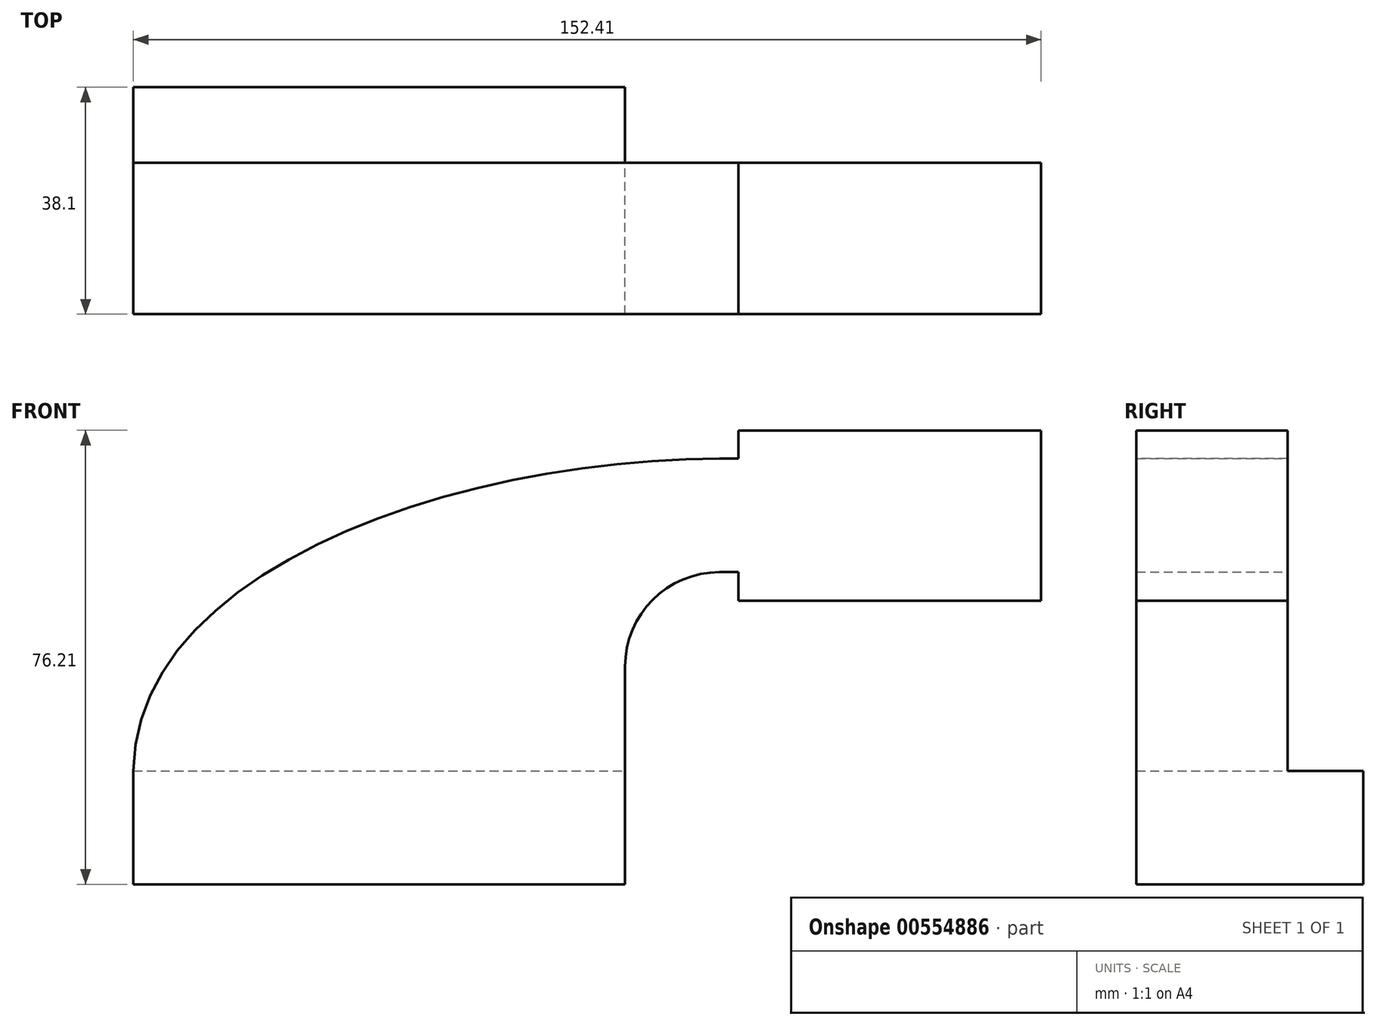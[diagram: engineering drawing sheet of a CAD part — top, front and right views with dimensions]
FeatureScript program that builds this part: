
annotation { "Feature Type Name" : "Feature", "Feature Type Description" : "" }
export const myFeature = defineFeature(function(context is Context, id is Id, definition is map)
    precondition{}
    {
        {
            var Q0;
            Q0=qCreatedBy(makeId("Front.planeOp"),FACE);
            var sketch = newSketch(context, id + "F0", { "sketchPlane" : qUnion([Q0])});
            skLineSegment(sketch, "E0.bottom", {"start": v(-41.28, 9.52) * mm, "end": v(41.27, 9.53) * mm});
            skLineSegment(sketch, "E0.top", {"start": v(-41.28, -9.52) * mm, "end": v(41.28, -9.52) * mm});
            skLineSegment(sketch, "E0.left", {"start": v(-41.28, 9.52) * mm, "end": v(-41.28, -9.53) * mm});
            skLineSegment(sketch, "E0.right", {"start": v(41.27, 9.53) * mm, "end": v(41.28, -9.52) * mm});
            skPoint(sketch, "E0.middle", {"position": v(0, 0) * mm});
            skLineSegment(sketch, "E1.bottom", {"start": v(60.32, 38.1) * mm, "end": v(111.12, 38.1) * mm});
            skLineSegment(sketch, "E1.top", {"start": v(60.32, 66.67) * mm, "end": v(111.12, 66.67) * mm});
            skLineSegment(sketch, "E1.left", {"start": v(60.32, 38.1) * mm, "end": v(60.32, 66.68) * mm});
            skLineSegment(sketch, "E1.right", {"start": v(111.12, 38.1) * mm, "end": v(111.12, 66.68) * mm});
            skPoint(sketch, "E1.middle", {"position": v(85.72, 52.39) * mm});
            skLineSegment(sketch, "E2", {"start": v(41.27, 9.53) * mm, "end": v(41.27, 27) * mm});
            skArc(sketch, "E3", {"start": v(41.27, 27) * mm, "mid": v(45.92, 38.23) * mm, "end": v(57.15, 42.88) * mm});
            skLineSegment(sketch, "E4", {"start": v(57.15, 42.88) * mm, "end": v(74.24, 42.88) * mm});
            skLineSegment(sketch, "E5.0", {"start": v(57.15, 61.93) * mm, "end": v(74.24, 61.93) * mm});
            skArc(sketch, "E5.1", {"start": v(22.22, 27) * mm, "mid": v(32.45, 51.7) * mm, "end": v(57.15, 61.93) * mm});
            skLineSegment(sketch, "E5.2", {"start": v(22.22, 9.53) * mm, "end": v(22.22, 27) * mm});
            skLineSegment(sketch, "E6", {"start": v(85.72, 38.1) * mm, "end": v(85.72, 66.67) * mm});
            skLineSegment(sketch, "E7", {"start": v(74.24, 61.93) * mm, "end": v(85.72, 61.93) * mm});
            skLineSegment(sketch, "E8", {"start": v(74.24, 42.88) * mm, "end": v(85.72, 42.88) * mm});
            skFitSpline(sketch, "E9", {"points": [v(-41.28, 9.52) * mm, v(57.15, 61.93) * mm], "startDerivative": vector(1.43, 103.54) * mm, "endDerivative": vector(128.32, -0.1) * mm});
            skSolve(sketch);
        }
        {
            var Q0;
            Q0=qCreatedBy(makeId("Front.planeOp"),FACE);
            var sketch = newSketch(context, id + "F1", { "sketchPlane" : qUnion([Q0])});
            skSolve(sketch);
        }
        {
            var Q0;
            Q0=makeQuery(id+"F0.imprint","IMPRINT",FACE,{"disambiguationData":[TD([[makeQuery(id+"F0.imprint","IMPRINT",EDGE,{"derivedFrom":sQuery(id+"F0.wireOp",EDGE,"E0.top")}),1.0]])]});
            extrude(context, id + "F2", {"entities" : qUnion([Q0]), "endBound" : BoundingType.SYMMETRIC, "depth" : 25.4 * mm, "offsetDistance" : 25.4 * mm});
        }
        {
            var Q0;
            Q0 = qSketchRegion(id + "F0XvRdL9u1ZFRl4_1", true);
            var Q1;
            Q1 = qSketchRegion(id + "F1", true);
            var Q2;
            Q2 = qSketchRegion(id + "F0", true);
            extrude(context, id + "F3", {"entities" : qUnion([Q0, Q1, Q2]), "operationType" : NewBodyOperationType.ADD, "depth" : 25.4 * mm, "offsetDistance" : 25.4 * mm});
        }
    });
